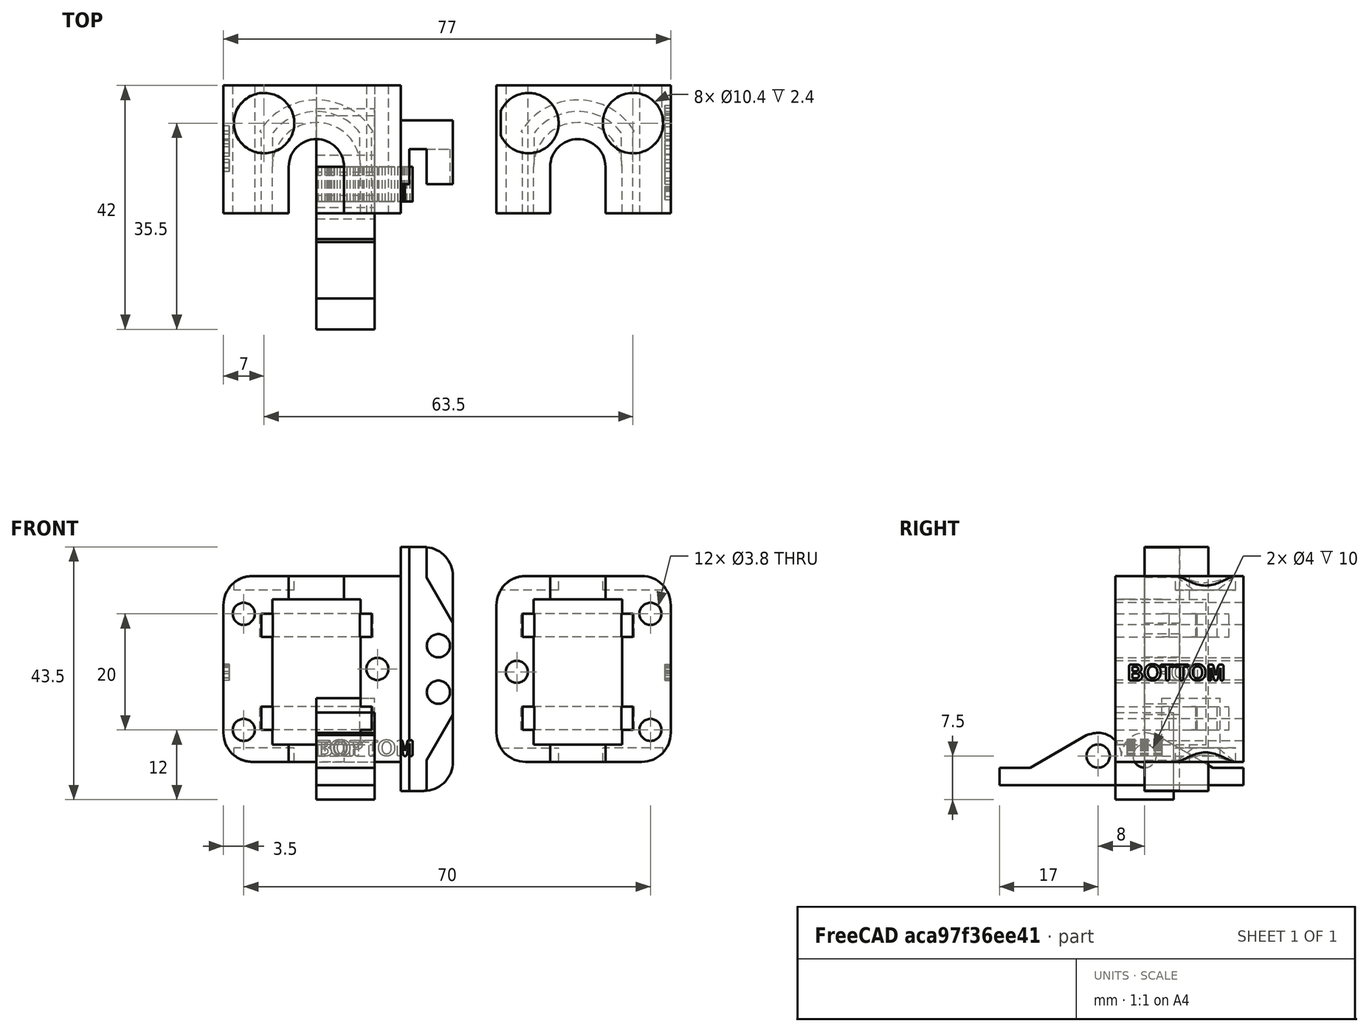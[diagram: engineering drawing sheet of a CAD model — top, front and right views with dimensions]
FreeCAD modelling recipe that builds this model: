
FCSTD DOCUMENT  (FreeCAD 0.16R6712 (Git))
Label: ParkingNozzleTransportSlider
License: All rights reserved
LicenseURL: http://en.wikipedia.org/wiki/All_rights_reserved
objects: Part::Cylinder×51, Part::MultiFuse×26, Part::Box×24, Part::Cut×19, Part::Feature×4, Part::Part2DObjectPython×2, Part::Extrusion×2
note: 128 computed .brp shape members not serialized (recipe doc carries the construction recipe); baked Part::Feature solids carry a one-line shape summary decoded from their .brp

FEATURE [Part::Box] Box  label="Würfel"
  Height = 10
  Length = 10
  Width = 10
FEATURE [Part::Cylinder] Cylinder  label="RJ4JP"
  Angle = 360
  Height = 25
  Placement = pos=(0,0,-0.5) rot=(0,0,1;0rad)
  Radius = 7.6
FEATURE [Part::Cylinder] Cylinder001  label="LinearStange8mm"
  Angle = 360
  Height = 44
  Placement = pos=(0,0,-10) rot=(0,0,1;0rad)
  Radius = 4.5
FEATURE [Part::Cylinder] Cylinder002  label="LinearSpacer9mm"
  Angle = 360
  Height = 34
  Placement = pos=(0,0,-5) rot=(0,0,1;0rad)
  Radius = 4.75
FEATURE [Part::MultiFuse] Fusion  label="GleitlagerAusspahrung"
  Shapes = -> [Cylinder,Cylinder002,Cylinder001]
FEATURE [Part::Cylinder] Cylinder003  label="Zylinder"
  Angle = 116
  Height = 4
  Placement = pos=(0,0,0) rot=(0,0,1;0.558505rad)
  Radius = 11.5
FEATURE [Part::Cylinder] Cylinder004  label="Zylinder001"
  Angle = 116
  Height = 4
  Placement = pos=(0,0,0) rot=(0,0,1;0.558505rad)
  Radius = 9.5
FEATURE [Part::Cut] Cut
  Base = -> Cylinder003
  Tool = -> Cylinder004
FEATURE [Part::Box] Box001  label="Würfel001"
  Height = 4
  Length = 2
  Placement = pos=(-9.5,-11,0) rot=(0,0,1;0rad)
  Width = 17
FEATURE [Part::Box] Box002  label="Würfel002"
  Height = 4
  Length = 2
  Placement = pos=(7.5,-11,0) rot=(0,0,1;0rad)
  Width = 17
FEATURE [Part::MultiFuse] Fusion001  label="KabelbinderAusspahrung002"
  Placement = pos=(0,0,18) rot=(0,0,1;0rad)
  Shapes = -> [Cut,Box002,Box001]
FEATURE [Part::Box] Box009  label="Würfel009"
  Height = 15
  Length = 10
  Placement = pos=(0,-8,-7.5) rot=(0,0,1;0rad)
  Width = 10
FEATURE [Part::Cylinder] Cylinder014  label="Zylinder008"
  Angle = 116
  Height = 4
  Placement = pos=(0,0,0) rot=(0,0,1;0.558505rad)
  Radius = 11.5
FEATURE [Part::Cylinder] Cylinder015  label="Zylinder009"
  Angle = 116
  Height = 4
  Placement = pos=(0,0,0) rot=(0,0,1;0.558505rad)
  Radius = 9.5
FEATURE [Part::Cut] Cut004
  Base = -> Cylinder014
  Tool = -> Cylinder015
FEATURE [Part::Box] Box010  label="Würfel010"
  Height = 4
  Length = 2
  Placement = pos=(-9.5,-11,0) rot=(0,0,1;0rad)
  Width = 17
FEATURE [Part::Box] Box011  label="Würfel011"
  Height = 4
  Length = 2
  Placement = pos=(7.5,-11,0) rot=(0,0,1;0rad)
  Width = 17
FEATURE [Part::MultiFuse] Fusion008  label="KabelbinderAusspahrung005"
  Placement = pos=(0,0,2) rot=(0,0,1;0rad)
  Shapes = -> [Cut004,Box011,Box010]
FEATURE [Part::Box] Box016  label="Block_A"
  Height = 32
  Length = 30.5
  Placement = pos=(-16,-8,-1) rot=(0,0,1;0rad)
  Width = 22
FEATURE [Part::Box] Box017  label="Würfel017"
  Height = 44
  Length = 9.5
  Placement = pos=(-4.75,-11,-10) rot=(0,0,1;0rad)
  Width = 11
FEATURE [Part::Box] Box018  label="Würfel018"
  Height = 25
  Length = 15.2
  Placement = pos=(-7.6,-11,-0.5) rot=(0,0,1;0rad)
  Width = 11
FEATURE [Part::MultiFuse] Fusion014  label="Schacht"
  Shapes = -> [Box017,Box018]
FEATURE [Part::MultiFuse] Fusion015  label="RJ4JP_Cut_Full_A"
  Shapes = -> [Fusion,Fusion001,Fusion008,Fusion014]
FEATURE [Part::Cylinder] Cylinder016  label="RJ4JP001"
  Angle = 360
  Height = 25
  Placement = pos=(0,0,-0.5) rot=(0,0,1;0rad)
  Radius = 7.6
FEATURE [Part::Cylinder] Cylinder017  label="LinearStange8mm001"
  Angle = 360
  Height = 44
  Placement = pos=(0,0,-10) rot=(0,0,1;0rad)
  Radius = 4.5
FEATURE [Part::Cylinder] Cylinder018  label="LinearSpacer9mm001"
  Angle = 360
  Height = 34
  Placement = pos=(0,0,-5) rot=(0,0,1;0rad)
  Radius = 4.75
FEATURE [Part::MultiFuse] Fusion016  label="GleitlagerAusspahrung001"
  Shapes = -> [Cylinder016,Cylinder018,Cylinder017]
FEATURE [Part::Cylinder] Cylinder019  label="Zylinder010"
  Angle = 116
  Height = 4
  Placement = pos=(0,0,0) rot=(0,0,1;0.558505rad)
  Radius = 11.5
FEATURE [Part::Cylinder] Cylinder020  label="Zylinder011"
  Angle = 116
  Height = 4
  Placement = pos=(0,0,0) rot=(0,0,1;0.558505rad)
  Radius = 9.5
FEATURE [Part::Cut] Cut005
  Base = -> Cylinder019
  Tool = -> Cylinder020
FEATURE [Part::Box] Box019  label="Würfel019"
  Height = 4
  Length = 2
  Placement = pos=(-9.5,-11,0) rot=(0,0,1;0rad)
  Width = 17
FEATURE [Part::Box] Box020  label="Würfel020"
  Height = 4
  Length = 2
  Placement = pos=(7.5,-11,0) rot=(0,0,1;0rad)
  Width = 17
FEATURE [Part::MultiFuse] Fusion017  label="KabelbinderAusspahrung006"
  Placement = pos=(0,0,18) rot=(0,0,1;0rad)
  Shapes = -> [Cut005,Box020,Box019]
FEATURE [Part::Cylinder] Cylinder021  label="Zylinder012"
  Angle = 116
  Height = 4
  Placement = pos=(0,0,0) rot=(0,0,1;0.558505rad)
  Radius = 11.5
FEATURE [Part::Cylinder] Cylinder022  label="Zylinder013"
  Angle = 116
  Height = 4
  Placement = pos=(0,0,0) rot=(0,0,1;0.558505rad)
  Radius = 9.5
FEATURE [Part::Cut] Cut006
  Base = -> Cylinder021
  Tool = -> Cylinder022
FEATURE [Part::Box] Box021  label="Würfel021"
  Height = 4
  Length = 2
  Placement = pos=(-9.5,-11,0) rot=(0,0,1;0rad)
  Width = 17
FEATURE [Part::Box] Box022  label="Würfel022"
  Height = 4
  Length = 2
  Placement = pos=(7.5,-11,0) rot=(0,0,1;0rad)
  Width = 17
FEATURE [Part::MultiFuse] Fusion018  label="KabelbinderAusspahrung007"
  Placement = pos=(0,0,2) rot=(0,0,1;0rad)
  Shapes = -> [Cut006,Box022,Box021]
FEATURE [Part::Box] Box023  label="Würfel023"
  Height = 44
  Length = 9.5
  Placement = pos=(-4.75,-11,-10) rot=(0,0,1;0rad)
  Width = 11
FEATURE [Part::Box] Box024  label="Würfel024"
  Height = 25
  Length = 15.2
  Placement = pos=(-7.6,-11,-0.5) rot=(0,0,1;0rad)
  Width = 11
FEATURE [Part::MultiFuse] Fusion019  label="Schacht001"
  Shapes = -> [Box023,Box024]
FEATURE [Part::MultiFuse] Fusion020  label="RJ4JP_Cut_Full_B"
  Placement = pos=(45,0,0) rot=(0,0,1;0rad)
  Shapes = -> [Fusion016,Fusion017,Fusion018,Fusion019]
FEATURE [Part::MultiFuse] Fusion021  label="X_RJ4JP_Cut"
  Placement = pos=(0,0,2.5) rot=(0,0,1;0rad)
  Shapes = -> [Fusion015,Fusion020]
FEATURE [Part::Box] Box025  label="Block_B"
  Height = 32
  Length = 30
  Placement = pos=(31,-8,-1) rot=(0,0,1;0rad)
  Width = 22
FEATURE [Part::Box] Box026  label="Würfel025"
  Height = 42
  Length = 11
  Placement = pos=(9,0,-6) rot=(0,0,1;0rad)
  Width = 9
FEATURE [Part::MultiFuse] Fusion022  label="GleitBlock"
  Shapes = -> [Box016,Box025]
FEATURE [Part::Cut] Cut007  label="GleitBloecke"
  Base = -> Fusion022
  Tool = -> Fusion021
FEATURE [Part::Cylinder] Cylinder025  label="Zylinder016"
  Angle = 360
  Height = 10
  Radius = 2
FEATURE [Part::Cylinder] Cylinder026  label="Zylinder017"
  Angle = 360
  Height = 10
  Radius = 4
FEATURE [Part::Cut] Cut009
  Base = -> Cylinder026
  Placement = pos=(0,-11,0) rot=(0,0,1;0rad)
  Tool = -> Cylinder025
FEATURE [Part::Box] Box028  label="Würfel027"
  Height = 10
  Length = 3
  Placement = pos=(2,-28,0) rot=(0,0,1;0rad)
  Width = 22
FEATURE [Part::Box] Box029  label="Würfel028"
  Height = 10
  Length = 1
  Placement = pos=(3.9,-26,0) rot=(0,0,1;0.523599rad)
  Width = 15
FEATURE [Part::Box] Box030  label="Würfel029"
  Height = 10
  Length = 3.3
  Placement = pos=(2,-21.5,0) rot=(0,0,1;0.523599rad)
  Width = 8
FEATURE [Part::Cylinder] Cylinder027  label="Zylinder018"
  Angle = 360
  Height = 10
  Placement = pos=(2,-15,0) rot=(0,0,1;0rad)
  Radius = 2
FEATURE [Part::Cylinder] Cylinder028  label="Zylinder019"
  Angle = 360
  Height = 10
  Placement = pos=(-2.73,-12.5,0) rot=(0,0,1;0rad)
  Radius = 1
FEATURE [Part::MultiFuse] Fusion023
  Shapes = -> [Cut009,Cylinder027,Cylinder028,Box028,Box029,Box030]
FEATURE [Part::Cylinder] Cylinder029  label="Zylinder020"
  Angle = 360
  Height = 10
  Radius = 2
FEATURE [Part::Cylinder] Cylinder030  label="Zylinder021"
  Angle = 360
  Height = 10
  Radius = 4
FEATURE [Part::Cut] Cut010
  Base = -> Cylinder030
  Placement = pos=(0,-11,0) rot=(0,0,1;0rad)
  Tool = -> Cylinder029
FEATURE [Part::Box] Box031  label="Würfel030"
  Height = 10
  Length = 3
  Placement = pos=(2,-28,0) rot=(0,0,1;0rad)
  Width = 20
FEATURE [Part::Box] Box032  label="Würfel031"
  Height = 10
  Length = 1
  Placement = pos=(3.9,-26,0) rot=(0,0,1;0.523599rad)
  Width = 15
FEATURE [Part::Box] Box033  label="Würfel032"
  Height = 10
  Length = 3.3
  Placement = pos=(2,-21.5,0) rot=(0,0,1;0.523599rad)
  Width = 8
FEATURE [Part::Cylinder] Cylinder031  label="Zylinder022"
  Angle = 360
  Height = 10
  Placement = pos=(2,-15,0) rot=(0,0,1;0rad)
  Radius = 2
FEATURE [Part::Cylinder] Cylinder032  label="Zylinder023"
  Angle = 360
  Height = 10
  Placement = pos=(-2.73,-12.5,0) rot=(0,0,1;0rad)
  Radius = 1
FEATURE [Part::MultiFuse] Fusion024
  Placement = pos=(0,-14,10) rot=(1,0,0;3.14159rad)
  Shapes = -> [Cut010,Cylinder031,Cylinder032,Box031,Box032,Box033]
FEATURE [Part::MultiFuse] Fusion025
  Shapes = -> [Fusion023,Fusion024]
FEATURE [Part::Cylinder] Cylinder033  label="Zylinder024"
  Angle = 360
  Height = 10
  Placement = pos=(2,-7,0) rot=(0,0,1;0rad)
  Radius = 2
FEATURE [Part::MultiFuse] Fusion026
  Placement = pos=(0,0,0) rot=(0,1,0;1.5708rad)
  Shapes = -> [Fusion025,Cylinder033]
FEATURE [Part::Feature] Fusion026001  label="Fusion027"
  Placement = pos=(14,6.5,8) rot=(-1,0,0;1.5708rad)
  shape: bbox 10 x 9 x 42 mm, 17 faces (baked)
FEATURE [Part::Cylinder] Cylinder034  label="Zylinder025"
  Angle = 360
  Height = 26
  Placement = pos=(-13,16,4.5) rot=(1,0,0;1.5708rad)
  Radius = 1.9
FEATURE [Part::Cylinder] Cylinder035  label="Zylinder026"
  Angle = 360
  Height = 26
  Placement = pos=(-13,16,24.5) rot=(1,0,0;1.5708rad)
  Radius = 1.9
FEATURE [Part::Cylinder] Cylinder036  label="Zylinder027"
  Angle = 360
  Height = 26
  Placement = pos=(10.5,16,15) rot=(1,0,0;1.5708rad)
  Radius = 1.9
FEATURE [Part::MultiFuse] Fusion026003
  Placement = pos=(0.5,0,0) rot=(0,0,1;0rad)
  Shapes = -> [Cylinder034,Cylinder035]
FEATURE [Part::Cylinder] Cylinder037  label="Zylinder028"
  Angle = 360
  Height = 26
  Placement = pos=(-13,16,4.5) rot=(1,0,0;1.5708rad)
  Radius = 1.9
FEATURE [Part::Cylinder] Cylinder038  label="Zylinder029"
  Angle = 360
  Height = 26
  Placement = pos=(-13,16,24.5) rot=(1,0,0;1.5708rad)
  Radius = 1.9
FEATURE [Part::MultiFuse] Fusion026004
  Placement = pos=(70.5,0,0) rot=(0,0,1;0rad)
  Shapes = -> [Cylinder037,Cylinder038]
FEATURE [Part::Cylinder] Cylinder039  label="Zylinder030"
  Angle = 360
  Height = 26
  Placement = pos=(34.5,16,14.5) rot=(1,0,0;1.5708rad)
  Radius = 1.9
FEATURE [Part::MultiFuse] Fusion026005  label="Bohrung"
  Shapes = -> [Cylinder036,Fusion026003,Fusion026004,Cylinder039]
FEATURE [Part::Part2DObjectPython] ShapeString  # Draft 2D object (typed FeaturePython)
  FontFile = <path>
  Size = 3
  String = TOP
  Tracking = 4
FEATURE [Part::Extrusion] Extrude
  Base = -> ShapeString
  Dir = (0,0,6)
  Placement = pos=(0,0,0) rot=(1,0,0;1.5708rad)
  Solid = false
FEATURE [Part::Part2DObjectPython] ShapeString001  # Draft 2D object (typed FeaturePython)
  FontFile = <path>
  Size = 3
  String = BOTTOM
  Tracking = 4
FEATURE [Part::Extrusion] Extrude001
  Base = -> ShapeString001
  Dir = (0,0,6)
  Placement = pos=(0,0,0) rot=(1,0,0;1.5708rad)
  Solid = false
FEATURE [Part::Feature] Extrude002
  Placement = pos=(-15,7,13) rot=(0,0,-1;1.5708rad)
  shape: bbox 6 x 7.877 x 2.835 mm, 76 faces, 3 solids (baked)
FEATURE [Part::Feature] Extrude001001  label="Extrude003"
  Placement = pos=(60,-6,13) rot=(0,0,1;1.5708rad)
  shape: bbox 6 x 16.23 x 2.835 mm, 171 faces, 6 solids (baked)
FEATURE [Part::MultiFuse] Fusion026006
  Shapes = -> [Extrude002,Extrude001001]
FEATURE [Part::Cut] Cut011002  label="Bloecke"
  Base = -> Cut007
  Tool = -> Fusion026006
FEATURE [Part::Cylinder] Cylinder041  label="Zylinder032"
  Angle = 360
  Height = 2.4
  Placement = pos=(-9,0,0) rot=(0,0,1;0rad)
  Radius = 5.2
FEATURE [Part::Cylinder] Cylinder042  label="Zylinder033"
  Angle = 360
  Height = 2.4
  Placement = pos=(54.5,0,0) rot=(0,0,1;0rad)
  Radius = 5.2
FEATURE [Part::Cylinder] Cylinder043  label="Zylinder034"
  Angle = 360
  Height = 2.4
  Placement = pos=(36.5,0,0) rot=(0,0,1;0rad)
  Radius = 5.2
FEATURE [Part::MultiFuse] Fusion026009  label="MagnetsLeft"
  Placement = pos=(0,7.5,28.6) rot=(0,0,1;0rad)
  Shapes = -> [Cylinder041,Cylinder043,Cylinder042]
FEATURE [Part::Cylinder] Cylinder044  label="Zylinder035"
  Angle = 360
  Height = 2.4
  Placement = pos=(-9,0,0) rot=(0,0,1;0rad)
  Radius = 5.2
FEATURE [Part::Cylinder] Cylinder045  label="Zylinder036"
  Angle = 360
  Height = 2.4
  Placement = pos=(54.5,0,0) rot=(0,0,1;0rad)
  Radius = 5.2
FEATURE [Part::Cylinder] Cylinder046  label="Zylinder037"
  Angle = 360
  Height = 2.4
  Placement = pos=(36.5,0,0) rot=(0,0,1;0rad)
  Radius = 5.2
FEATURE [Part::MultiFuse] Fusion026010  label="MagnetsRight"
  Placement = pos=(0,7.5,-1) rot=(0,0,1;0rad)
  Shapes = -> [Cylinder044,Cylinder046,Cylinder045]
FEATURE [Part::MultiFuse] Fusion026011  label="Magnets"
  Shapes = -> [Fusion026009,Fusion026010]
FEATURE [Part::Cylinder] Cylinder047  label="Zylinder038"
  Angle = 90
  Height = 40
  Placement = pos=(33,25,29) rot=(1,0,0;1.5708rad)
  Radius = 8
FEATURE [Part::Cylinder] Cylinder048  label="Zylinder039"
  Angle = 90
  Height = 40
  Placement = pos=(33,25,29) rot=(1,0,0;1.5708rad)
  Radius = 5
FEATURE [Part::Cut] Cut011004002
  Base = -> Cylinder047
  Placement = pos=(65,0,-7) rot=(0,-1,0;1.5708rad)
  Tool = -> Cylinder048
FEATURE [Part::Cylinder] Cylinder049  label="Zylinder040"
  Angle = 90
  Height = 40
  Placement = pos=(33,25,29) rot=(1,0,0;1.5708rad)
  Radius = 8
FEATURE [Part::Cylinder] Cylinder050  label="Zylinder041"
  Angle = 90
  Height = 40
  Placement = pos=(33,25,29) rot=(1,0,0;1.5708rad)
  Radius = 5
FEATURE [Part::Cut] Cut011004003
  Base = -> Cylinder049
  Placement = pos=(69,0,33) rot=(0,1,0;3.14159rad)
  Tool = -> Cylinder050
FEATURE [Part::Cylinder] Cylinder051  label="Zylinder042"
  Angle = 90
  Height = 40
  Placement = pos=(33,25,29) rot=(1,0,0;1.5708rad)
  Radius = 8
FEATURE [Part::Cylinder] Cylinder052  label="Zylinder043"
  Angle = 90
  Height = 40
  Placement = pos=(33,25,29) rot=(1,0,0;1.5708rad)
  Radius = 5
FEATURE [Part::Cut] Cut011004004
  Base = -> Cylinder051
  Placement = pos=(18,0,-7) rot=(0,-1,0;1.5708rad)
  Tool = -> Cylinder052
FEATURE [Part::Cylinder] Cylinder053  label="Zylinder044"
  Angle = 90
  Height = 40
  Placement = pos=(33,25,29) rot=(1,0,0;1.5708rad)
  Radius = 8
FEATURE [Part::Cylinder] Cylinder054  label="Zylinder045"
  Angle = 90
  Height = 40
  Placement = pos=(33,25,29) rot=(1,0,0;1.5708rad)
  Radius = 5
FEATURE [Part::Cut] Cut011004005
  Base = -> Cylinder053
  Placement = pos=(22,0,33) rot=(0,1,0;3.14159rad)
  Tool = -> Cylinder054
FEATURE [Part::Cylinder] Cylinder055  label="Zylinder046"
  Angle = 90
  Height = 40
  Placement = pos=(33,25,29) rot=(1,0,0;1.5708rad)
  Radius = 8
FEATURE [Part::Cylinder] Cylinder056  label="Zylinder047"
  Angle = 90
  Height = 40
  Placement = pos=(33,25,29) rot=(1,0,0;1.5708rad)
  Radius = 5
FEATURE [Part::Cut] Cut011004006
  Base = -> Cylinder055
  Placement = pos=(23,0,-3) rot=(0,0,1;0rad)
  Tool = -> Cylinder056
FEATURE [Part::Cylinder] Cylinder057  label="Zylinder048"
  Angle = 90
  Height = 40
  Placement = pos=(33,25,29) rot=(1,0,0;1.5708rad)
  Radius = 8
FEATURE [Part::Cylinder] Cylinder058  label="Zylinder049"
  Angle = 90
  Height = 40
  Placement = pos=(33,25,29) rot=(1,0,0;1.5708rad)
  Radius = 5
FEATURE [Part::Cut] Cut011004007
  Base = -> Cylinder057
  Placement = pos=(-10.5,0,32) rot=(0,1,0;1.5708rad)
  Tool = -> Cylinder058
FEATURE [Part::Cylinder] Cylinder059  label="Zylinder050"
  Angle = 90
  Height = 40
  Placement = pos=(33,25,29) rot=(1,0,0;1.5708rad)
  Radius = 8
FEATURE [Part::Cylinder] Cylinder060  label="Zylinder051"
  Angle = 90
  Height = 40
  Placement = pos=(33,25,29) rot=(1,0,0;1.5708rad)
  Radius = 5
FEATURE [Part::Cut] Cut011004008
  Base = -> Cylinder059
  Placement = pos=(27,0,37) rot=(0,1,0;1.5708rad)
  Tool = -> Cylinder060
FEATURE [Part::Cylinder] Cylinder061  label="Zylinder052"
  Angle = 90
  Height = 40
  Placement = pos=(33,25,29) rot=(1,0,0;1.5708rad)
  Radius = 8
FEATURE [Part::Cylinder] Cylinder062  label="Zylinder053"
  Angle = 90
  Height = 40
  Placement = pos=(33,25,29) rot=(1,0,0;1.5708rad)
  Radius = 5
FEATURE [Part::Cut] Cut011004009
  Base = -> Cylinder061
  Placement = pos=(-14.5,0,2) rot=(0,0,1;0rad)
  Tool = -> Cylinder062
FEATURE [Part::MultiFuse] Fusion026012  label="RoundEdges"
  Shapes = -> [Cut011004002,Cut011004003,Cut011004009,Cut011004008,Cut011004006,Cut011004007,Cut011004004,Cut011004005]
FEATURE [Part::Cut] Cut011004010
  Base = -> Box026
  Placement = pos=(14.5,17,0) rot=(0,0,-1;1.5708rad)
  Tool = -> Fusion026001
FEATURE [Part::Box] Box035  label="Würfel034"
  Height = 2
  Length = 3
  Placement = pos=(21,-7,14) rot=(0,0,1;0rad)
  Width = 10
FEATURE [Part::Cut] Cut011004011  label="BeltFixation"
  Base = -> Cut011004010
  Tool = -> Box035
FEATURE [Part::MultiFuse] Fusion026013  label="Mount_Full"
  Shapes = -> [Cut011002,Cut011004011]
FEATURE [Part::MultiFuse] Fusion026014  label="To_Cut"
  Shapes = -> [Fusion026012,Fusion026011,Fusion026005]
FEATURE [Part::Cut] Cut011004012  label="TransportSlider"
  Base = -> Fusion026013
  Tool = -> Fusion026014
FEATURE [Part::Feature] Cut011004012001  label="TransportSlider_export"
  shape: bbox 77 x 22 x 42 mm, 374 faces, 2 solids (baked)
note: 2 file-system paths scrubbed to <path> (originals preserved in the JSON sidecar)
